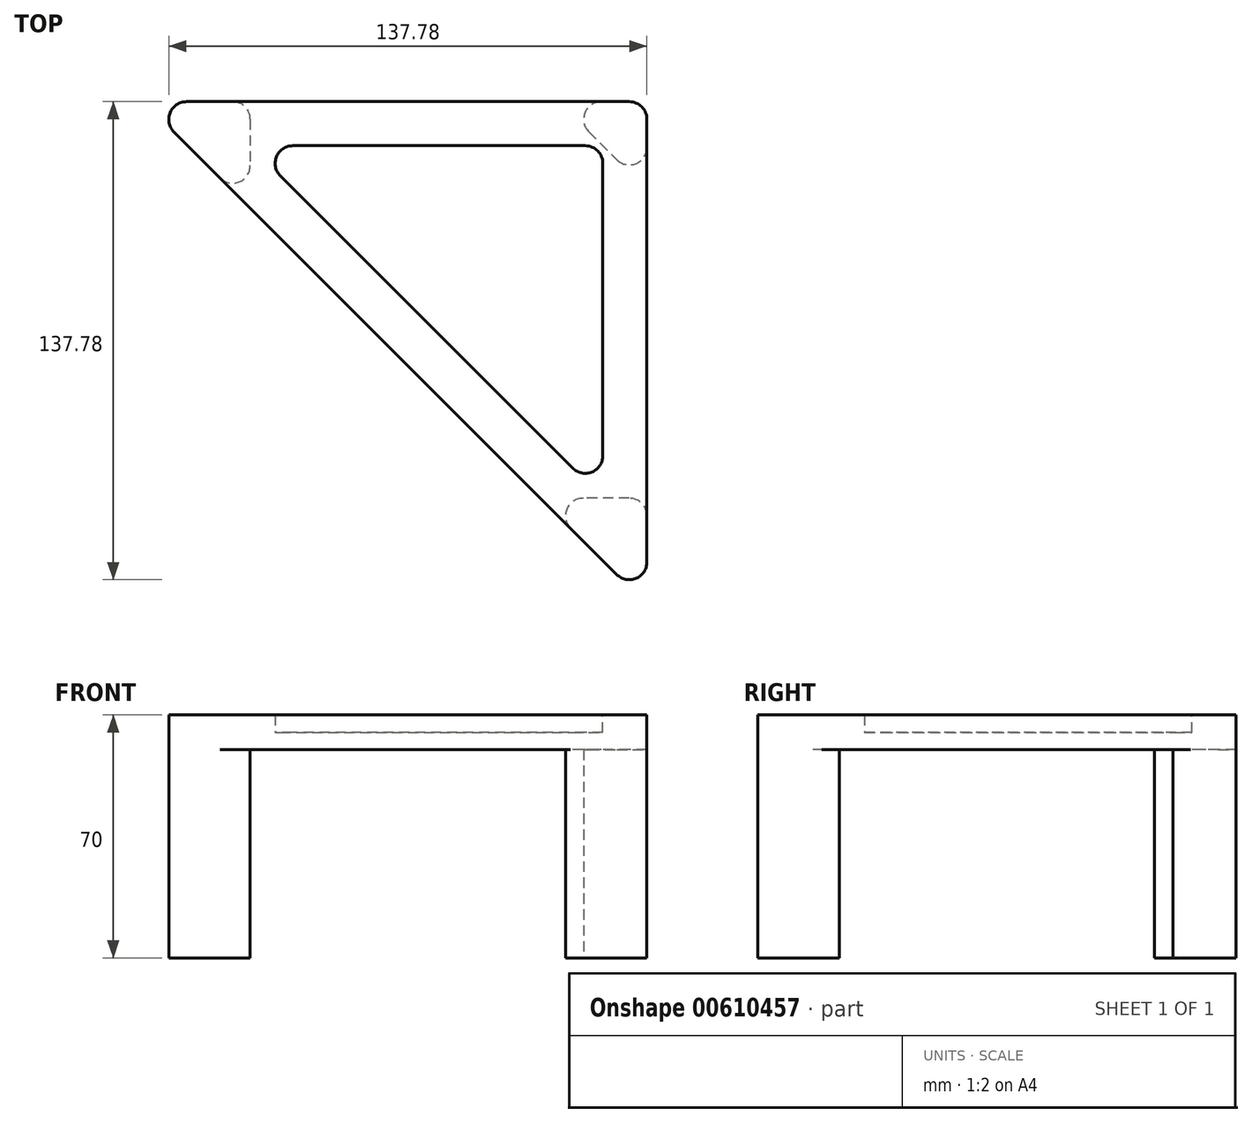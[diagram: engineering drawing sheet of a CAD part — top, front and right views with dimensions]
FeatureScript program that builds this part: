
annotation { "Feature Type Name" : "Feature", "Feature Type Description" : "" }
export const myFeature = defineFeature(function(context is Context, id is Id, definition is map)
    precondition{}
    {
        {
            var Q0;
            Q0=qCreatedBy(makeId("Top.planeOp"),FACE);
            var sketch = newSketch(context, id + "F0", { "sketchPlane" : qUnion([Q0])});
            skLineSegment(sketch, "E0.bottom", {"start": v(50.8, -50.8) * mm, "end": v(-50.8, -50.8) * mm, "construction": true});
            skLineSegment(sketch, "E0.top", {"start": v(50.8, 50.8) * mm, "end": v(-50.8, 50.8) * mm, "construction": true});
            skLineSegment(sketch, "E0.left", {"start": v(50.8, -50.8) * mm, "end": v(50.8, 50.8) * mm, "construction": true});
            skLineSegment(sketch, "E0.right", {"start": v(-50.8, -50.8) * mm, "end": v(-50.8, 50.8) * mm, "construction": true});
            skPoint(sketch, "E0.middle", {"position": v(0, 0) * mm});
            skLineSegment(sketch, "E1", {"start": v(-50.8, 50.8) * mm, "end": v(50.8, -50.8) * mm, "construction": true});
            skLineSegment(sketch, "E2.0", {"start": v(63.5, 63.5) * mm, "end": v(-81.46, 63.5) * mm});
            skLineSegment(sketch, "E2.1", {"start": v(63.5, -81.46) * mm, "end": v(63.5, 63.5) * mm});
            skLineSegment(sketch, "E2.2", {"start": v(-81.46, 63.5) * mm, "end": v(63.5, -81.46) * mm});
            skLineSegment(sketch, "E3", {"start": v(-50.8, 63.5) * mm, "end": v(-50.8, 32.84) * mm});
            skLineSegment(sketch, "E4", {"start": v(63.5, -50.8) * mm, "end": v(32.84, -50.8) * mm});
            skLineSegment(sketch, "E5", {"start": v(50.8, 50.8) * mm, "end": v(63.5, 38.1) * mm});
            skLineSegment(sketch, "E6", {"start": v(50.8, 50.8) * mm, "end": v(38.1, 63.5) * mm});
            skSolve(sketch);
        }
        {
            var Q0;
            Q0=makeQuery(id+"F0.imprint","IMPRINT",FACE,{"disambiguationData":[TD([[makeQuery(id+"F0.imprint","IMPRINT",EDGE,{"derivedFrom":sQuery(id+"F0.wireOp",EDGE,"E2.0")}),1.0]])]});
            var Q1;
            Q1=makeQuery(id+"F0.imprint","IMPRINT",FACE,{"disambiguationData":[TD([[makeQuery(id+"F0.imprint","IMPRINT",EDGE,{"derivedFrom":sQuery(id+"F0.wireOp",EDGE,"2JG5F3nT-iPg3-Z0lb-hLKr-0JxkAQGCaj8A")}),1.0]])]});
            var Q2;
            Q2=makeQuery(id+"F0.imprint","IMPRINT",FACE,{"disambiguationData":[TD([[makeQuery(id+"F0.imprint","IMPRINT",EDGE,{"derivedFrom":sQuery(id+"F0.wireOp",EDGE,"3MCKx9vc-RhU7-Ryyq-vuTJ-toGGR69b1FhZ")}),1.0]])]});
            var Q3;
            Q3=makeQuery(id+"F0.imprint","IMPRINT",FACE,{"disambiguationData":[TD([[makeQuery(id+"F0.imprint","IMPRINT",EDGE,{"derivedFrom":sQuery(id+"F0.wireOp",EDGE,"HfQweQlb-YUWH-AAmf-f3BP-ZiMPkcvuaOqB")}),1.0]])]});
            var Q4;
            {var subQ0=sQuery(id+"F0.wireOp",EDGE,"E3");Q4=makeQuery(id+"F0.imprint","IMPRINT",FACE,{"disambiguationData":[TD([[makeQuery(id+"F0.imprint","IMPRINT",EDGE,{"derivedFrom":subQ0}),1.0]])]});}
            var Q5;
            {var subQ4=sQuery(id+"F0.wireOp",EDGE,"E5");Q5=makeQuery(id+"F0.imprint","IMPRINT",FACE,{"disambiguationData":[TD([[makeQuery(id+"F0.imprint","IMPRINT",EDGE,{"derivedFrom":subQ4}),1.0]])]});}
            var Q6;
            {var subQ3=sQuery(id+"F0.wireOp",EDGE,"E4");Q6=makeQuery(id+"F0.imprint","IMPRINT",FACE,{"disambiguationData":[TD([[makeQuery(id+"F0.imprint","IMPRINT",EDGE,{"derivedFrom":subQ3}),1.0]])]});}
            extrude(context, id + "F1", {"entities" : qUnion([Q0, Q1, Q2, Q3, Q4, Q5, Q6]), "depth" : 10 * mm, "offsetDistance" : 25.4 * mm});
        }
        {
            var Q0;
            Q0=makeQuery(id+"F1.opExtrude","SWEPT_EDGE",EDGE,{"disambiguationData":[OSD([sQuery(id+"F0.wireOp",EDGE,"E2.1"),sQuery(id+"F0.wireOp",EDGE,"E2.2")])]});
            var Q1;
            Q1=makeQuery(id+"F1.opExtrude","SWEPT_EDGE",EDGE,{"disambiguationData":[OSD([sQuery(id+"F0.wireOp",EDGE,"E2.0"),sQuery(id+"F0.wireOp",EDGE,"E2.2")])]});
            var Q2;
            Q2=makeQuery(id+"F1.opExtrude","SWEPT_EDGE",EDGE,{"disambiguationData":[OSD([sQuery(id+"F0.wireOp",EDGE,"E2.0"),sQuery(id+"F0.wireOp",EDGE,"E2.1")])]});
            fillet(context, id + "F2", {"entities" : qUnion([Q0, Q1, Q2]), "radius" : 5.08 * mm, "tangentPropagation" : true, "allowEdgeOverflow" : false});
        }
        {
            var Q0;
            Q0=makeQuery(id+"F0.imprint","IMPRINT",FACE,{"disambiguationData":[TD([[makeQuery(id+"F0.imprint","IMPRINT",EDGE,{"derivedFrom":sQuery(id+"F0.wireOp",EDGE,"E2.0")}),1.0]])]});
            var sketch = newSketch(context, id + "F3", { "sketchPlane" : qUnion([Q0])});
            skLineSegment(sketch, "E7.0", {"start": v(-81.46, 63.5) * mm, "end": v(63.5, -81.46) * mm});
            skLineSegment(sketch, "E8", {"start": v(-8.98, -8.98) * mm, "end": v(-3.66, -3.66) * mm});
            skLineSegment(sketch, "E9", {"start": v(-3.66, -3.66) * mm, "end": v(14.3, -21.62) * mm});
            skLineSegment(sketch, "E10", {"start": v(-3.66, -3.66) * mm, "end": v(-21.62, 14.3) * mm});
            skLineSegment(sketch, "E11", {"start": v(-21.62, 14.3) * mm, "end": v(-26.94, 8.98) * mm});
            skLineSegment(sketch, "E12", {"start": v(14.3, -21.62) * mm, "end": v(8.98, -26.94) * mm});
            skSolve(sketch);
        }
        {
            var Q0;
            {var subQ3=sQuery(id+"F0.wireOp",EDGE,"E4");Q0=makeQuery(id+"F0.imprint","IMPRINT",FACE,{"disambiguationData":[TD([[makeQuery(id+"F0.imprint","IMPRINT",EDGE,{"derivedFrom":subQ3}),1.0]])]});}
            var Q1;
            {var subQ4=sQuery(id+"F0.wireOp",EDGE,"E5");Q1=makeQuery(id+"F0.imprint","IMPRINT",FACE,{"disambiguationData":[TD([[makeQuery(id+"F0.imprint","IMPRINT",EDGE,{"derivedFrom":subQ4}),1.0]])]});}
            var Q2;
            {var subQ2=sQuery(id+"F0.wireOp",EDGE,"E3");var subQ4=makeQuery(id+"F0.imprint","IMPRINT",EDGE,{"derivedFrom":subQ2});Q2=makeQuery(id+"F3.imprint","IMPRINT",FACE,{"disambiguationData":[TD([[makeQuery(id+"F3.imprint","IMPRINT",EDGE,{"derivedFrom":subQ4}),-1.0]])]});}
            extrude(context, id + "F4", {"entities" : qUnion([Q0, Q1, Q2]), "operationType" : NewBodyOperationType.ADD, "oppositeDirection" : true, "depth" : 60 * mm, "offsetDistance" : 25.4 * mm});
        }
        {
            var Q0;
            Q0=makeQuery(id+"F4.opExtrude","SWEPT_EDGE",EDGE,{"disambiguationData":[OSD([sQuery(id+"F0.wireOp",EDGE,"E2.0"),sQuery(id+"F3.wireOp",EDGE,"E7.0")])]});
            var Q1;
            Q1=makeQuery(id+"F4.opExtrude","SWEPT_EDGE",EDGE,{"disambiguationData":[OSD([sQuery(id+"F0.wireOp",EDGE,"E2.1"),sQuery(id+"F0.wireOp",EDGE,"E2.2")])]});
            var Q2;
            Q2=makeQuery(id+"F4.opExtrude","SWEPT_EDGE",EDGE,{"disambiguationData":[OSD([sQuery(id+"F0.wireOp",EDGE,"E2.0"),sQuery(id+"F0.wireOp",EDGE,"E2.1")])]});
            var Q3;
            Q3=makeQuery(id+"F4.opExtrude","SWEPT_EDGE",EDGE,{"disambiguationData":[OSD([sQuery(id+"F0.wireOp",EDGE,"E2.2"),sQuery(id+"F0.wireOp",EDGE,"E4")])]});
            var Q4;
            Q4=makeQuery(id+"F4.opExtrude","SWEPT_EDGE",EDGE,{"disambiguationData":[OSD([sQuery(id+"F0.wireOp",EDGE,"E3"),sQuery(id+"F3.wireOp",EDGE,"E7.0")])]});
            var Q5;
            Q5=makeQuery(id+"F4.opExtrude","SWEPT_EDGE",EDGE,{"disambiguationData":[OSD([sQuery(id+"F0.wireOp",EDGE,"E2.0"),sQuery(id+"F0.wireOp",EDGE,"E3")])]});
            var Q6;
            Q6=makeQuery(id+"F4.opExtrude","SWEPT_EDGE",EDGE,{"disambiguationData":[OSD([sQuery(id+"F0.wireOp",EDGE,"E2.0"),sQuery(id+"F0.wireOp",EDGE,"E6")])]});
            var Q7;
            Q7=makeQuery(id+"F4.opExtrude","SWEPT_EDGE",EDGE,{"disambiguationData":[OSD([sQuery(id+"F0.wireOp",EDGE,"E2.1"),sQuery(id+"F0.wireOp",EDGE,"E5")])]});
            var Q8;
            Q8=makeQuery(id+"F4.opExtrude","SWEPT_EDGE",EDGE,{"disambiguationData":[OSD([sQuery(id+"F0.wireOp",EDGE,"E2.1"),sQuery(id+"F0.wireOp",EDGE,"E4")])]});
            fillet(context, id + "F5", {"entities" : qUnion([Q0, Q1, Q2, Q3, Q4, Q5, Q6, Q7, Q8]), "tangentPropagation" : true, "radius" : 5.08 * mm, "defaultsChanged" : false, "vertexSettings" : [], "allowEdgeOverflow" : false});
        }
        {
            var Q0;
            Q0=makeQuery(id+"F1.opExtrude","CAP_FACE",FACE,{"disambiguationData":[OSD([sQuery(id+"F0.wireOp",EDGE,"E2.0"),sQuery(id+"F0.wireOp",EDGE,"E2.1"),sQuery(id+"F0.wireOp",EDGE,"E2.2")])],"isStart":false});
            var sketch = newSketch(context, id + "F6", { "sketchPlane" : qUnion([Q0])});
            skLineSegment(sketch, "E13.0", {"start": v(-50.8, 50.8) * mm, "end": v(50.8, -50.8) * mm});
            skLineSegment(sketch, "E13.1", {"start": v(50.8, -50.8) * mm, "end": v(50.8, 50.8) * mm});
            skLineSegment(sketch, "E13.2", {"start": v(50.8, 50.8) * mm, "end": v(-50.8, 50.8) * mm});
            skSolve(sketch);
        }
        {
            var Q0;
            Q0=makeQuery(id+"F6.imprint","IMPRINT",FACE,{"disambiguationData":[TD([[makeQuery(id+"F6.imprint","IMPRINT",EDGE,{"derivedFrom":sQuery(id+"F6.wireOp",EDGE,"E13.0")}),1.0]])]});
            extrude(context, id + "F7", {"entities" : qUnion([Q0]), "operationType" : NewBodyOperationType.REMOVE, "oppositeDirection" : true, "depth" : 5.08 * mm, "offsetDistance" : 25.4 * mm});
        }
        {
            var Q0;
            Q0=makeQuery(id+"F7.boolean.opBoolean","COPY",EDGE,{"derivedFrom":makeQuery(id+"F7.opExtrude","SWEPT_EDGE",EDGE,{"disambiguationData":[OSD([sQuery(id+"F6.wireOp",EDGE,"E13.1"),sQuery(id+"F6.wireOp",EDGE,"E13.2")])]})});
            var Q1;
            Q1=makeQuery(id+"F7.boolean.opBoolean","COPY",EDGE,{"derivedFrom":makeQuery(id+"F7.opExtrude","SWEPT_EDGE",EDGE,{"disambiguationData":[OSD([sQuery(id+"F6.wireOp",EDGE,"E13.0"),sQuery(id+"F6.wireOp",EDGE,"E13.2")])]})});
            var Q2;
            Q2=makeQuery(id+"F7.boolean.opBoolean","COPY",EDGE,{"derivedFrom":makeQuery(id+"F7.opExtrude","SWEPT_EDGE",EDGE,{"disambiguationData":[OSD([sQuery(id+"F6.wireOp",EDGE,"E13.0"),sQuery(id+"F6.wireOp",EDGE,"E13.1")])]})});
            fillet(context, id + "F8", {"entities" : qUnion([Q0, Q1, Q2]), "tangentPropagation" : true, "radius" : 5.08 * mm, "defaultsChanged" : false, "vertexSettings" : [], "allowEdgeOverflow" : false});
        }
    });
